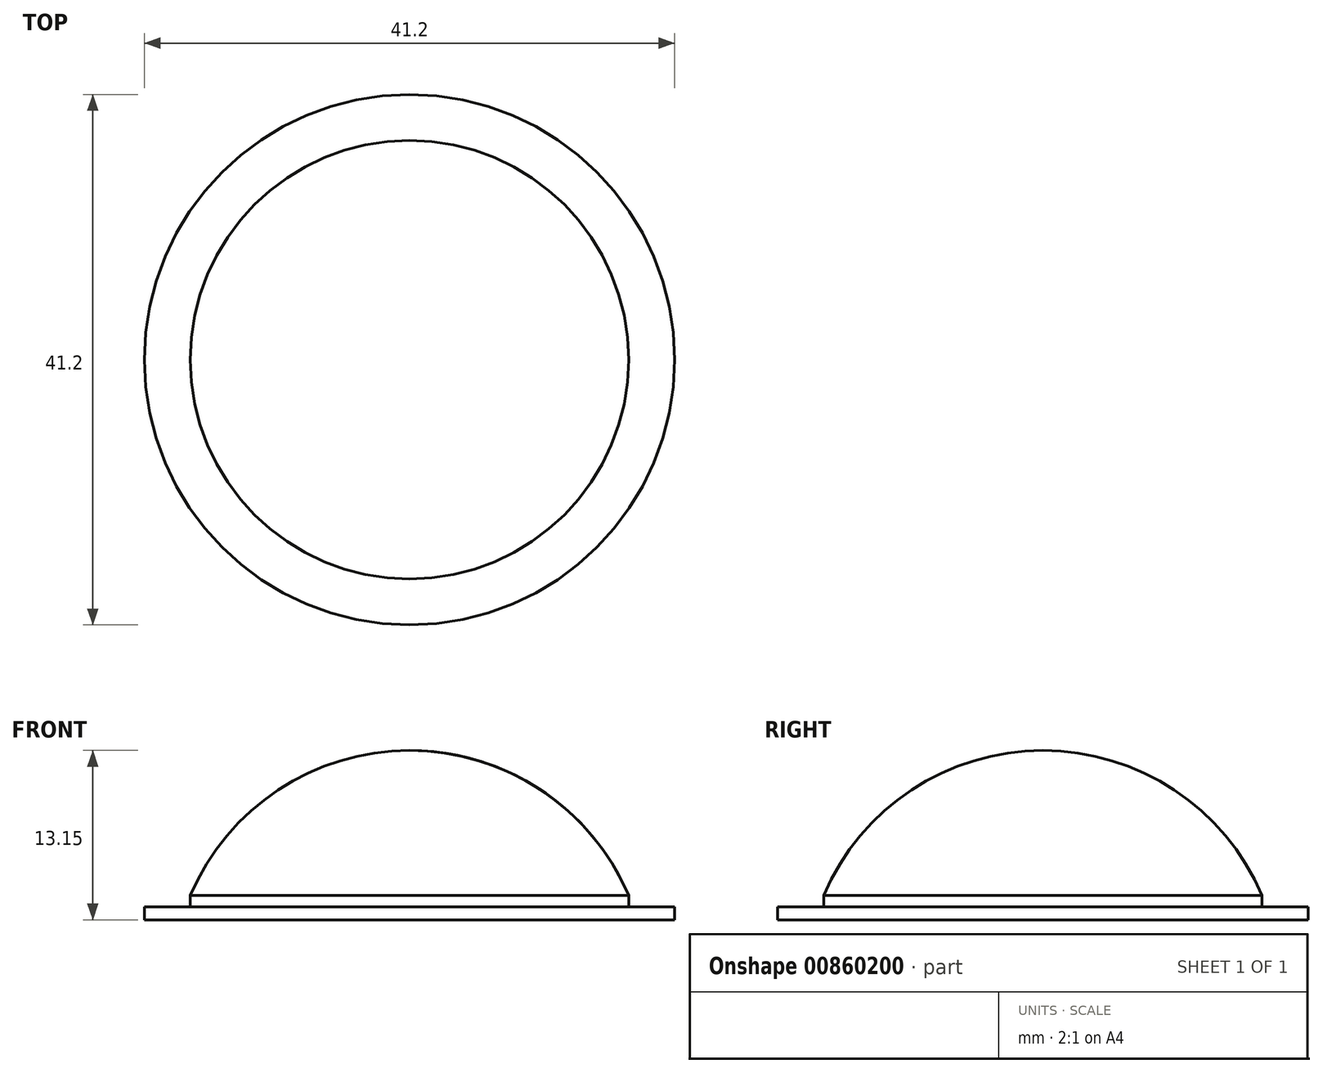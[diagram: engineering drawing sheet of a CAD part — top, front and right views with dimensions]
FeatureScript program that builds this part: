
annotation { "Feature Type Name" : "Feature", "Feature Type Description" : "" }
export const myFeature = defineFeature(function(context is Context, id is Id, definition is map)
    precondition{}
    {
        {
            var Q0;
            Q0=qCreatedBy(makeId("Front.planeOp"),FACE);
            var sketch = newSketch(context, id + "F0", { "sketchPlane" : qUnion([Q0])});
            skArc(sketch, "E0.0", {"start": v(17.02, 4.91) * mm, "mid": v(10.2, 13.1) * mm, "end": v(0, 16.17) * mm});
            skLineSegment(sketch, "E1", {"start": v(20.6, 4.02) * mm, "end": v(18.6, 4.02) * mm});
            skLineSegment(sketch, "E2", {"start": v(20.6, 4.02) * mm, "end": v(20.6, 3.02) * mm});
            skLineSegment(sketch, "E3", {"start": v(20.6, 3.02) * mm, "end": v(0, 3.02) * mm});
            skLineSegment(sketch, "E4", {"start": v(0, 3.02) * mm, "end": v(0, 16.17) * mm});
            skLineSegment(sketch, "E5", {"start": v(18.6, 4.02) * mm, "end": v(17.02, 4.02) * mm});
            skLineSegment(sketch, "E6", {"start": v(17.02, 4.02) * mm, "end": v(17.02, 4.91) * mm});
            skSolve(sketch);
        }
        {
            var Q0;
            Q0 = qSketchRegion(id + "F0", true);
            var Q1;
            Q1=sQuery(id+"F0.wireOp",EDGE,"E4");
            revolve(context, id + "F1", {"surfaceOperationType" : NewSurfaceOperationType.NEW, "entities" : qUnion([Q0]), "axis" : qUnion([Q1]), "revolveType" : RevolveType.FULL});
        }
    });
